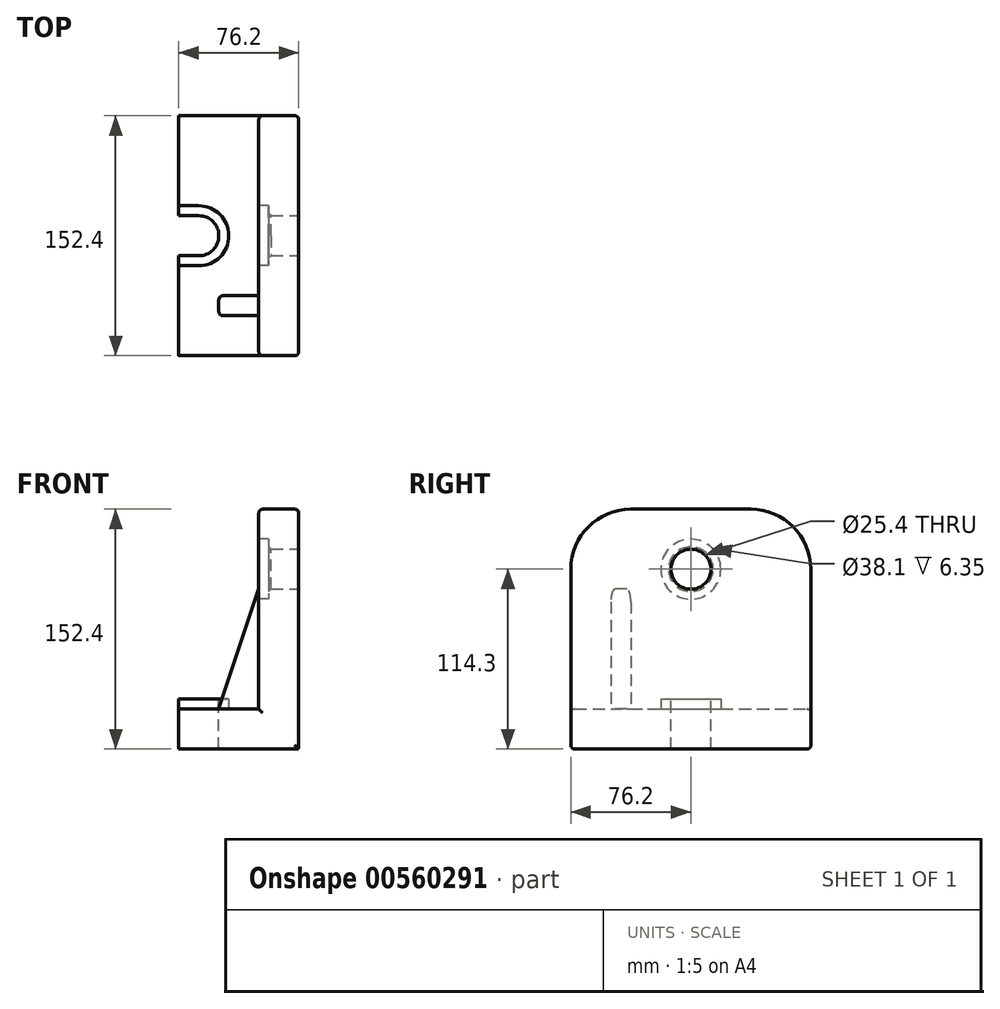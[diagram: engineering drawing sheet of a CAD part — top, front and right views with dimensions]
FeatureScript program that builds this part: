
annotation { "Feature Type Name" : "Feature", "Feature Type Description" : "" }
export const myFeature = defineFeature(function(context is Context, id is Id, definition is map)
    precondition{}
    {
        {
            var Q0;
            Q0=qCreatedBy(makeId("Front.planeOp"),FACE);
            var sketch = newSketch(context, id + "F0", { "sketchPlane" : qUnion([Q0])});
            skLineSegment(sketch, "E0", {"start": v(-50.8, 0) * mm, "end": v(-50.8, -25.4) * mm});
            skLineSegment(sketch, "E1", {"start": v(-50.8, -25.4) * mm, "end": v(25.4, -25.4) * mm});
            skLineSegment(sketch, "E2", {"start": v(25.4, -25.4) * mm, "end": v(25.4, 127) * mm});
            skLineSegment(sketch, "E3", {"start": v(25.4, 127) * mm, "end": v(0, 127) * mm});
            skLineSegment(sketch, "E4", {"start": v(0, 127) * mm, "end": v(0, 0) * mm});
            skLineSegment(sketch, "E5", {"start": v(0, 0) * mm, "end": v(-50.8, 0) * mm});
            skSolve(sketch);
        }
        {
            var Q0;
            Q0=makeQuery(id+"F0.imprint","IMPRINT",FACE,{"disambiguationData":[TD([[makeQuery(id+"F0.imprint","IMPRINT",EDGE,{"derivedFrom":sQuery(id+"F0.wireOp",EDGE,"E0")}),1.0]])]});
            extrude(context, id + "F1", {"entities" : qUnion([Q0]), "endBound" : BoundingType.SYMMETRIC, "depth" : 152.4 * mm, "offsetDistance" : 25.4 * mm});
        }
        {
            var Q0;
            Q0=makeQuery(id+"F1.opExtrude","SWEPT_FACE",FACE,{"disambiguationData":[OSD([sQuery(id+"F0.wireOp",EDGE,"E2")])]});
            var sketch = newSketch(context, id + "F2", { "sketchPlane" : qUnion([Q0])});
            skCircle(sketch, "E6", {"center": v(0, 88.9) * mm, "radius": 12.7 * mm});
            skSolve(sketch);
        }
        {
            var Q0;
            Q0=makeQuery(id+"F2.imprint","IMPRINT",FACE,{"disambiguationData":[TD([[makeQuery(id+"F2.imprint","IMPRINT",EDGE,{"derivedFrom":sQuery(id+"F2.wireOp",EDGE,"E6")}),1.0]])]});
            extrude(context, id + "F3", {"entities" : qUnion([Q0]), "operationType" : NewBodyOperationType.REMOVE, "endBound" : BoundingType.THROUGH_ALL, "oppositeDirection" : true, "depth" : 25.4 * mm, "offsetDistance" : 25.4 * mm});
        }
        {
            var Q0;
            Q0=makeQuery(id+"F1.opExtrude","SWEPT_FACE",FACE,{"disambiguationData":[OSD([sQuery(id+"F0.wireOp",EDGE,"E5")])]});
            var sketch = newSketch(context, id + "F4", { "sketchPlane" : qUnion([Q0])});
            skArc(sketch, "E7", {"start": v(-38.1, -12.7) * mm, "mid": v(-25.4, 0) * mm, "end": v(-38.1, 12.7) * mm});
            skLineSegment(sketch, "E8", {"start": v(-38.1, 12.7) * mm, "end": v(-50.8, 12.7) * mm});
            skLineSegment(sketch, "E9", {"start": v(-38.1, -12.7) * mm, "end": v(-50.8, -12.7) * mm});
            skSolve(sketch);
        }
        {
            var Q0;
            Q0=makeQuery(id+"F4.imprint","IMPRINT",FACE,{"disambiguationData":[TD([[makeQuery(id+"F4.imprint","IMPRINT",EDGE,{"derivedFrom":sQuery(id+"F4.wireOp",EDGE,"E7")}),1.0]])]});
            extrude(context, id + "F5", {"entities" : qUnion([Q0]), "operationType" : NewBodyOperationType.REMOVE, "endBound" : BoundingType.THROUGH_ALL, "oppositeDirection" : true, "depth" : 25.4 * mm, "offsetDistance" : 25.4 * mm});
        }
        {
            var Q0;
            Q0=makeQuery(id+"F1.opExtrude","SWEPT_FACE",FACE,{"disambiguationData":[OSD([sQuery(id+"F0.wireOp",EDGE,"E4")])]});
            var sketch = newSketch(context, id + "F6", { "sketchPlane" : qUnion([Q0])});
            skLineSegment(sketch, "E10.0", {"start": v(76.2, 127) * mm, "end": v(-76.2, 127) * mm});
            skLineSegment(sketch, "E11.0", {"start": v(-76.2, 127) * mm, "end": v(-76.2, 0) * mm});
            skLineSegment(sketch, "E12.0", {"start": v(76.2, 127) * mm, "end": v(76.2, 0) * mm});
            skArc(sketch, "E13", {"start": v(76.2, 88.9) * mm, "mid": v(65.04, 115.84) * mm, "end": v(38.1, 127) * mm});
            skArc(sketch, "E14", {"start": v(-38.1, 127) * mm, "mid": v(-65.04, 115.84) * mm, "end": v(-76.2, 88.9) * mm});
            skSolve(sketch);
        }
        {
            var Q0;
            Q0=makeQuery(id+"F1.opExtrude","SWEPT_FACE",FACE,{"disambiguationData":[OSD([sQuery(id+"F0.wireOp",EDGE,"E4")])]});
            var sketch = newSketch(context, id + "F7", { "sketchPlane" : qUnion([Q0])});
            skCircle(sketch, "E15", {"center": v(0, 88.9) * mm, "radius": 19.05 * mm});
            skSolve(sketch);
        }
        {
            var Q0;
            Q0 = qSketchRegion(id + "F7", true);
            extrude(context, id + "F8", {"entities" : qUnion([Q0]), "operationType" : NewBodyOperationType.REMOVE, "oppositeDirection" : true, "depth" : 6.35 * mm, "offsetDistance" : 25.4 * mm});
        }
        {
            var Q0;
            Q0=makeQuery(id+"F1.opExtrude","CAP_FACE",FACE,{"disambiguationData":[OSD([sQuery(id+"F0.wireOp",EDGE,"E0"),sQuery(id+"F0.wireOp",EDGE,"E1"),sQuery(id+"F0.wireOp",EDGE,"E2"),sQuery(id+"F0.wireOp",EDGE,"E3"),sQuery(id+"F0.wireOp",EDGE,"E4"),sQuery(id+"F0.wireOp",EDGE,"E5")])],"isStart":false});
            cPlane(context, id + "F9", {"entities" : qUnion([Q0]), "cplaneType" : CPlaneType.OFFSET, "offset" : 44.45 * mm, "width" : 152.4 * mm, "height" : 152.4 * mm});
        }
        {
            var Q0;
            Q0=makeQuery(id+"F1.opExtrude","SWEPT_FACE",FACE,{"disambiguationData":[OSD([sQuery(id+"F0.wireOp",EDGE,"E2")])]});
            cPlane(context, id + "F10", {"entities" : qUnion([Q0]), "cplaneType" : CPlaneType.OFFSET, "offset" : 12.7 * mm, "oppositeDirection" : true, "width" : 152.4 * mm, "height" : 152.4 * mm});
        }
        {
            var Q0;
            Q0=qCreatedBy(id+"F9.planeOp",FACE);
            var sketch = newSketch(context, id + "F11", { "sketchPlane" : qUnion([Q0])});
            skLineSegment(sketch, "E16.0", {"start": v(0, 88.9) * mm, "end": v(0, 0) * mm});
            skLineSegment(sketch, "E17.0", {"start": v(0, 0) * mm, "end": v(-50.8, 0) * mm});
            skLineSegment(sketch, "E18", {"start": v(0, 76.2) * mm, "end": v(-25.4, 0) * mm});
            skSolve(sketch);
        }
        {
            var Q0;
            Q0 = qSketchRegion(id + "F11", true);
            extrude(context, id + "F12", {"entities" : qUnion([Q0]), "operationType" : NewBodyOperationType.ADD, "oppositeDirection" : true, "depth" : 82.55 * mm, "offsetDistance" : 25.4 * mm, "hasSecondDirection" : true, "secondDirectionOppositeDirection" : true, "secondDirectionDepth" : 69.85 * mm});
        }
        {
            var Q0;
            Q0=makeQuery(id+"F1.opExtrude","CAP_EDGE",EDGE,{"disambiguationData":[OSD([sQuery(id+"F0.wireOp",EDGE,"E3")])],"isStart":true});
            var Q1;
            Q1=makeQuery(id+"F1.opExtrude","CAP_EDGE",EDGE,{"disambiguationData":[OSD([sQuery(id+"F0.wireOp",EDGE,"E3")])],"isStart":false});
            fillet(context, id + "F13", {"entities" : qUnion([Q0, Q1]), "radius" : 38.1 * mm, "tangentPropagation" : true, "allowEdgeOverflow" : false});
        }
        {
            var Q0;
            Q0=makeQuery(id+"F8.boolean.opBoolean","INTERSECT",EDGE,{"derivedFrom":[makeQuery(id+"F3.boolean.opBoolean","COPY",FACE,{"derivedFrom":makeQuery(id+"F3.opExtrude","SWEPT_FACE",FACE,{"disambiguationData":[OSD([sQuery(id+"F2.wireOp",EDGE,"E6")])]})}),makeQuery(id+"F8.opExtrude","CAP_FACE",FACE,{"disambiguationData":[OSD([sQuery(id+"F7.wireOp",EDGE,"E15")])],"isStart":false})]});
            var Q1;
            Q1=makeQuery(id+"F8.boolean.opBoolean","COPY",EDGE,{"derivedFrom":makeQuery(id+"F8.opExtrude","CAP_EDGE",EDGE,{"disambiguationData":[OSD([sQuery(id+"F7.wireOp",EDGE,"E15")])],"isStart":true})});
            chamfer(context, id + "F14", {"entities" : qUnion([Q0, Q1]), "width" : 1.52 * mm, "tangentPropagation" : true});
        }
        {
            var Q0;
            Q0=makeQuery(id+"F1.opExtrude","SWEPT_FACE",FACE,{"disambiguationData":[OSD([sQuery(id+"F0.wireOp",EDGE,"E5")])]});
            var sketch = newSketch(context, id + "F15", { "sketchPlane" : qUnion([Q0])});
            skArc(sketch, "E19", {"start": v(-38.1, -19.05) * mm, "mid": v(-19.05, 0) * mm, "end": v(-38.1, 19.05) * mm});
            skLineSegment(sketch, "E20", {"start": v(-38.1, 19.05) * mm, "end": v(-50.8, 19.05) * mm});
            skLineSegment(sketch, "E21", {"start": v(-38.1, -19.05) * mm, "end": v(-50.8, -19.05) * mm});
            skSolve(sketch);
        }
        {
            var Q0;
            Q0=makeQuery(id+"F15.imprint","IMPRINT",FACE,{"disambiguationData":[TD([[makeQuery(id+"F15.imprint","IMPRINT",EDGE,{"derivedFrom":sQuery(id+"F15.wireOp",EDGE,"E19")}),1.0]])]});
            extrude(context, id + "F16", {"entities" : qUnion([Q0]), "operationType" : NewBodyOperationType.ADD, "depth" : 6.35 * mm, "offsetDistance" : 25.4 * mm});
        }
        {
            var Q0;
            Q0=makeQuery(id+"F16.opExtrude","CAP_EDGE",EDGE,{"disambiguationData":[OSD([sQuery(id+"F15.wireOp",EDGE,"E20")])],"isStart":true});
            var Q1;
            Q1=makeQuery(id+"F12.opExtrude","CAP_EDGE",EDGE,{"disambiguationData":[OSD([sQuery(id+"F11.wireOp",EDGE,"E18")])],"isStart":false});
            var Q2;
            Q2=makeQuery(id+"F12.opExtrude","CAP_EDGE",EDGE,{"disambiguationData":[OSD([sQuery(id+"F11.wireOp",EDGE,"E18")])],"isStart":true});
            var Q3;
            Q3=makeQuery(id+"FrSk7gVqGYAmJDW_1.1.F12.opExtrude","CAP_EDGE",EDGE,{"disambiguationData":[OSD([sQuery(id+"F11.wireOp",EDGE,"E18")])],"isStart":true});
            var Q4;
            Q4=makeQuery(id+"FrSk7gVqGYAmJDW_1.1.F12.opExtrude","CAP_EDGE",EDGE,{"disambiguationData":[OSD([sQuery(id+"F11.wireOp",EDGE,"E18")])],"isStart":false});
            var Q5;
            Q5=makeQuery(id+"F1.opExtrude","CAP_EDGE",EDGE,{"disambiguationData":[OSD([sQuery(id+"F0.wireOp",EDGE,"E4")])],"isStart":false});
            var Q6;
            Q6=makeQuery(id+"F1.opExtrude","CAP_EDGE",EDGE,{"disambiguationData":[OSD([sQuery(id+"F0.wireOp",EDGE,"E2")])],"isStart":false});
            var Q7;
            Q7=makeQuery(id+"F1.opExtrude","CAP_EDGE",EDGE,{"disambiguationData":[OSD([sQuery(id+"F0.wireOp",EDGE,"E5")])],"isStart":false});
            var Q8;
            Q8=makeQuery(id+"F1.opExtrude","CAP_EDGE",EDGE,{"disambiguationData":[OSD([sQuery(id+"F0.wireOp",EDGE,"E1")])],"isStart":false});
            var Q9;
            Q9=makeQuery(id+"F1.opExtrude","CAP_EDGE",EDGE,{"disambiguationData":[OSD([sQuery(id+"F0.wireOp",EDGE,"E5")])],"isStart":true});
            var Q10;
            Q10=makeQuery(id+"F1.opExtrude","CAP_EDGE",EDGE,{"disambiguationData":[OSD([sQuery(id+"F0.wireOp",EDGE,"E1")])],"isStart":true});
            fillet(context, id + "F17", {"entities" : qUnion([Q0, Q1, Q2, Q3, Q4, Q5, Q6, Q7, Q8, Q9, Q10]), "radius" : 2.54 * mm, "tangentPropagation" : true, "allowEdgeOverflow" : false});
        }
    });
